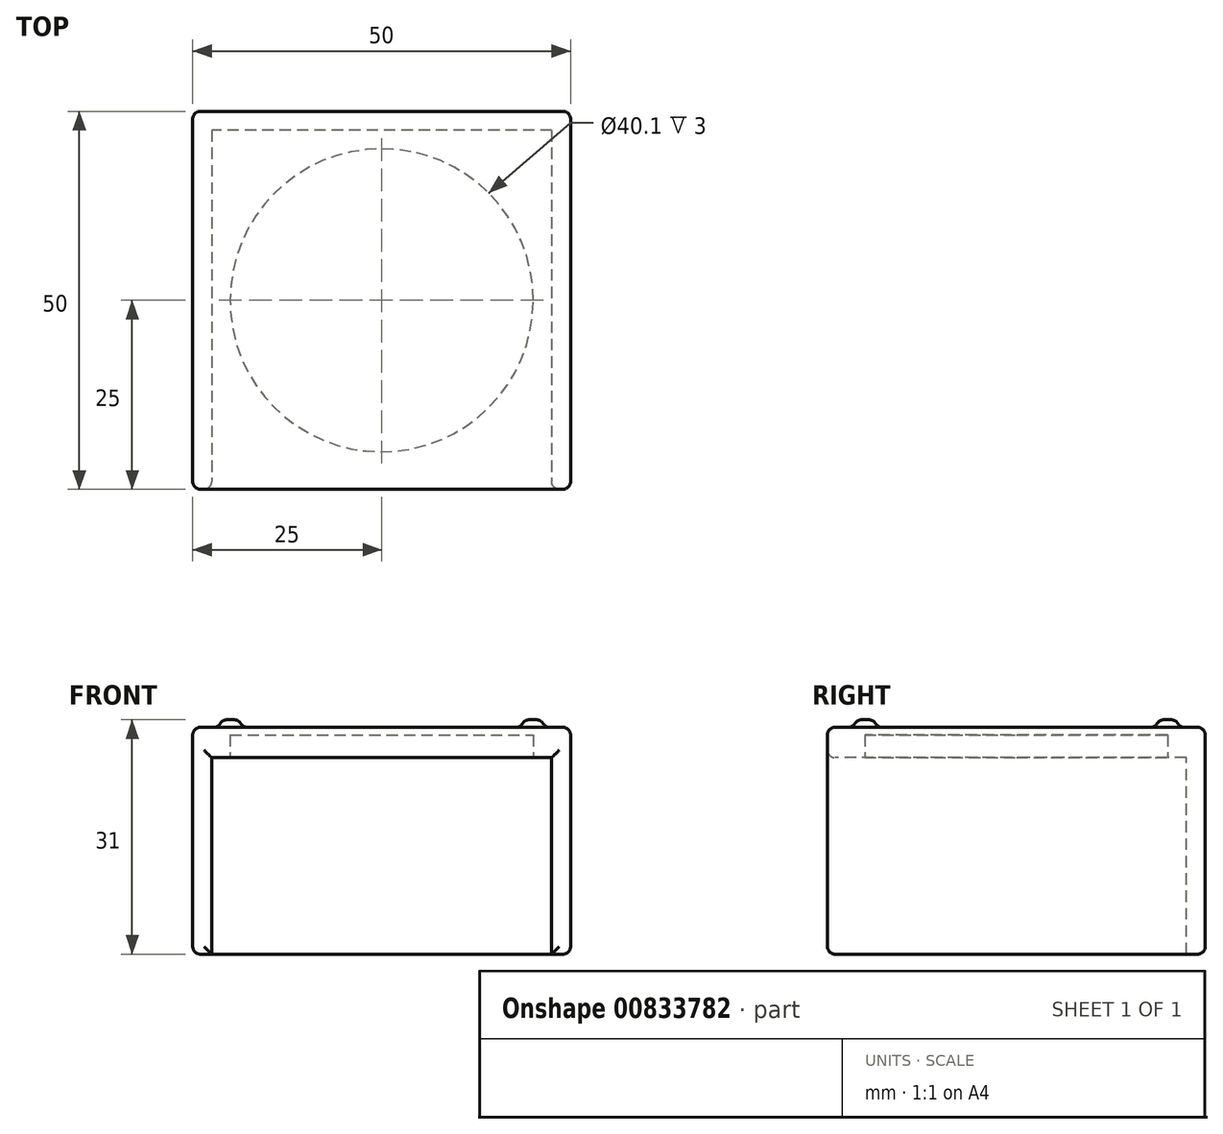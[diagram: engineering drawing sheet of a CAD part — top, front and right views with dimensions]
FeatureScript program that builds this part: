
annotation { "Feature Type Name" : "Feature", "Feature Type Description" : "" }
export const myFeature = defineFeature(function(context is Context, id is Id, definition is map)
    precondition{}
    {
        {
            var Q0;
            Q0=qCreatedBy(makeId("Front.planeOp"),FACE);
            var sketch = newSketch(context, id + "F0", { "sketchPlane" : qUnion([Q0])});
            skLineSegment(sketch, "E0.bottom", {"start": v(25, -15) * mm, "end": v(-25, -15) * mm});
            skLineSegment(sketch, "E0.top", {"start": v(25, 15) * mm, "end": v(-25, 15) * mm});
            skLineSegment(sketch, "E0.left", {"start": v(25, -15) * mm, "end": v(25, 15) * mm});
            skLineSegment(sketch, "E0.right", {"start": v(-25, -15) * mm, "end": v(-25, 15) * mm});
            skPoint(sketch, "E0.middle", {"position": v(0, 0) * mm});
            skSolve(sketch);
        }
        {
            var Q0;
            Q0 = qSketchRegion(id + "F0", true);
            extrude(context, id + "F1", {"entities" : qUnion([Q0]), "depth" : 25 * mm, "offsetDistance" : 25 * mm, "hasSecondDirection" : true, "secondDirectionOppositeDirection" : true, "secondDirectionDepth" : 25 * mm});
        }
        {
            var Q0;
            Q0=makeQuery(id+"F1.opExtrude","CAP_FACE",FACE,{"disambiguationData":[OSD([sQuery(id+"F0.wireOp",EDGE,"E0.bottom"),sQuery(id+"F0.wireOp",EDGE,"E0.top"),sQuery(id+"F0.wireOp",EDGE,"E0.left"),sQuery(id+"F0.wireOp",EDGE,"E0.right")])],"isStart":false});
            var sketch = newSketch(context, id + "F2", { "sketchPlane" : qUnion([Q0])});
            skLineSegment(sketch, "E1.bottom", {"start": v(-22.5, -15) * mm, "end": v(22.5, -15) * mm});
            skLineSegment(sketch, "E1.top", {"start": v(-22.5, 11) * mm, "end": v(22.5, 11) * mm});
            skLineSegment(sketch, "E1.left", {"start": v(-22.5, -15) * mm, "end": v(-22.5, 11) * mm});
            skLineSegment(sketch, "E1.right", {"start": v(22.5, -15) * mm, "end": v(22.5, 11) * mm});
            skSolve(sketch);
        }
        {
            var Q0;
            Q0 = qSketchRegion(id + "F2", true);
            extrude(context, id + "F3", {"entities" : qUnion([Q0]), "operationType" : NewBodyOperationType.REMOVE, "oppositeDirection" : true, "depth" : 47.5 * mm, "offsetDistance" : 25 * mm});
        }
        {
            var Q0;
            Q0=makeQuery(id+"F3.boolean.opBoolean","COPY",FACE,{"derivedFrom":makeQuery(id+"F3.opExtrude","SWEPT_FACE",FACE,{"disambiguationData":[OSD([sQuery(id+"F2.wireOp",EDGE,"E1.top")])]})});
            var sketch = newSketch(context, id + "F4", { "sketchPlane" : qUnion([Q0])});
            skCircle(sketch, "E2", {"center": v(0, 0) * mm, "radius": 20.05 * mm});
            skSolve(sketch);
        }
        {
            var Q0;
            Q0 = qSketchRegion(id + "F4", true);
            extrude(context, id + "F5", {"entities" : qUnion([Q0]), "operationType" : NewBodyOperationType.REMOVE, "oppositeDirection" : true, "depth" : 3 * mm, "offsetDistance" : 25 * mm});
        }
        {
            var Q0;
            Q0=makeQuery(id+"F1.opExtrude","SWEPT_FACE",FACE,{"disambiguationData":[OSD([sQuery(id+"F0.wireOp",EDGE,"E0.top")])]});
            var sketch = newSketch(context, id + "F6", { "sketchPlane" : qUnion([Q0])});
            skCircle(sketch, "E3", {"center": v(-20, 20) * mm, "radius": 1.5 * mm});
            skCircle(sketch, "E4", {"center": v(20, 20) * mm, "radius": 1.5 * mm});
            skCircle(sketch, "E5", {"center": v(20, -20) * mm, "radius": 1.5 * mm});
            skCircle(sketch, "E6", {"center": v(-20, -20) * mm, "radius": 1.5 * mm});
            skSolve(sketch);
        }
        {
            var Q0;
            Q0 = qSketchRegion(id + "F6", true);
            extrude(context, id + "F7", {"entities" : qUnion([Q0]), "operationType" : NewBodyOperationType.ADD, "depth" : 1 * mm, "offsetDistance" : 25 * mm});
        }
        {
            var Q0;
            Q0=makeQuery(id+"F7.opExtrude","CAP_EDGE",EDGE,{"disambiguationData":[OSD([sQuery(id+"F6.wireOp",EDGE,"E6")])],"isStart":false});
            var Q1;
            Q1=makeQuery(id+"F7.opExtrude","CAP_EDGE",EDGE,{"disambiguationData":[OSD([sQuery(id+"F6.wireOp",EDGE,"E5")])],"isStart":false});
            var Q2;
            Q2=makeQuery(id+"F7.opExtrude","CAP_EDGE",EDGE,{"disambiguationData":[OSD([sQuery(id+"F6.wireOp",EDGE,"E4")])],"isStart":false});
            var Q3;
            Q3=makeQuery(id+"F7.opExtrude","CAP_EDGE",EDGE,{"disambiguationData":[OSD([sQuery(id+"F6.wireOp",EDGE,"E3")])],"isStart":false});
            fillet(context, id + "F8", {"entities" : qUnion([Q0, Q1, Q2, Q3]), "tangentPropagation" : true, "radius" : 1 * mm, "defaultsChanged" : false, "vertexSettings" : [], "allowEdgeOverflow" : false});
        }
        {
            var Q0;
            Q0=makeQuery(id+"F1.opExtrude","SWEPT_FACE",FACE,{"disambiguationData":[OSD([sQuery(id+"F0.wireOp",EDGE,"E0.top")])]});
            var Q1;
            Q1=makeQuery(id+"F1.opExtrude","CAP_FACE",FACE,{"disambiguationData":[OSD([sQuery(id+"F0.wireOp",EDGE,"E0.bottom"),sQuery(id+"F0.wireOp",EDGE,"E0.top"),sQuery(id+"F0.wireOp",EDGE,"E0.left"),sQuery(id+"F0.wireOp",EDGE,"E0.right")])],"isStart":false});
            var Q2;
            Q2=makeQuery(id+"F1.opExtrude","SWEPT_FACE",FACE,{"disambiguationData":[OSD([sQuery(id+"F0.wireOp",EDGE,"E0.left")])]});
            var Q3;
            Q3=makeQuery(id+"F1.opExtrude","CAP_FACE",FACE,{"disambiguationData":[OSD([sQuery(id+"F0.wireOp",EDGE,"E0.bottom"),sQuery(id+"F0.wireOp",EDGE,"E0.top"),sQuery(id+"F0.wireOp",EDGE,"E0.left"),sQuery(id+"F0.wireOp",EDGE,"E0.right")])],"isStart":true});
            var Q4;
            Q4=makeQuery(id+"F1.opExtrude","SWEPT_FACE",FACE,{"disambiguationData":[OSD([sQuery(id+"F0.wireOp",EDGE,"E0.right")])]});
            fillet(context, id + "F9", {"entities" : qUnion([Q0, Q1, Q2, Q3, Q4]), "tangentPropagation" : true, "radius" : 1 * mm, "defaultsChanged" : false, "vertexSettings" : [], "allowEdgeOverflow" : false});
        }
    });
